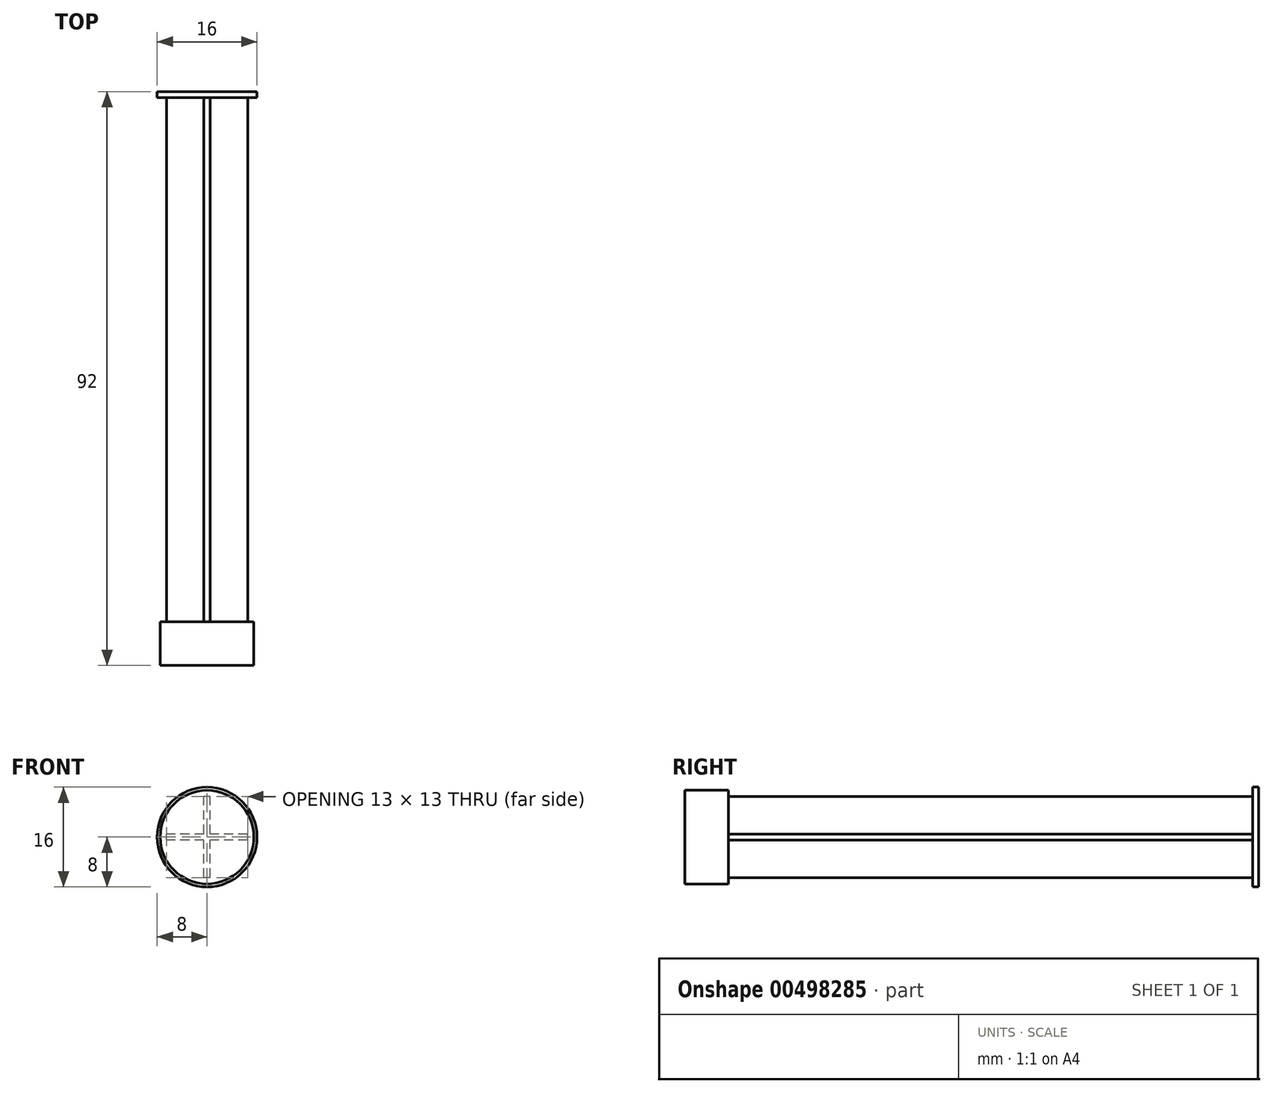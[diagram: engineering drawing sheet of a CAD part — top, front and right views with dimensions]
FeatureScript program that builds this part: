
annotation { "Feature Type Name" : "Feature", "Feature Type Description" : "" }
export const myFeature = defineFeature(function(context is Context, id is Id, definition is map)
    precondition{}
    {
        {
            var Q0;
            Q0=qCreatedBy(makeId("Front.planeOp"),FACE);
            var sketch = newSketch(context, id + "F0", { "sketchPlane" : qUnion([Q0])});
            skCircle(sketch, "E0", {"center": v(0, 0) * mm, "radius": 8 * mm});
            skSolve(sketch);
        }
        {
            var Q0;
            Q0 = qSketchRegion(id + "F0", true);
            var Q1;
            Q1=makeQuery(id+"F0.imprint","IMPRINT",FACE,{"disambiguationData":[TD([[makeQuery(id+"F0.imprint","IMPRINT",EDGE,{"derivedFrom":sQuery(id+"F0.wireOp",EDGE,"E0")}),1.0]])]});
            extrude(context, id + "F1", {"entities" : qUnion([Q0, Q1]), "depth" : 1 * mm});
        }
        {
            var Q0;
            Q0=makeQuery(id+"F1.opExtrude","CAP_FACE",FACE,{"disambiguationData":[OSD([sQuery(id+"F0.wireOp",EDGE,"E0")])],"isStart":false});
            var sketch = newSketch(context, id + "F2", { "sketchPlane" : qUnion([Q0])});
            skLineSegment(sketch, "E1", {"start": v(-6.5, 0) * mm, "end": v(6.5, 0) * mm});
            skLineSegment(sketch, "E2", {"start": v(0, 6.5) * mm, "end": v(0, -6.5) * mm});
            skLineSegment(sketch, "E3", {"start": v(-0.5, 0) * mm, "end": v(0.5, 0) * mm});
            skLineSegment(sketch, "E4", {"start": v(0, 0.5) * mm, "end": v(0, -0.5) * mm});
            skLineSegment(sketch, "E5.bottom", {"start": v(6.5, -0.5) * mm, "end": v(-6.5, -0.5) * mm});
            skLineSegment(sketch, "E5.top", {"start": v(6.5, 0.5) * mm, "end": v(-6.5, 0.5) * mm});
            skLineSegment(sketch, "E5.left", {"start": v(6.5, -0.5) * mm, "end": v(6.5, 0.5) * mm});
            skLineSegment(sketch, "E5.right", {"start": v(-6.5, -0.5) * mm, "end": v(-6.5, 0.5) * mm});
            skPoint(sketch, "E5.middle", {"position": v(0, 0) * mm});
            skLineSegment(sketch, "E6.bottom", {"start": v(0.5, -6.5) * mm, "end": v(-0.5, -6.5) * mm});
            skLineSegment(sketch, "E6.top", {"start": v(0.5, 6.5) * mm, "end": v(-0.5, 6.5) * mm});
            skLineSegment(sketch, "E6.left", {"start": v(0.5, -6.5) * mm, "end": v(0.5, 6.5) * mm});
            skLineSegment(sketch, "E6.right", {"start": v(-0.5, -6.5) * mm, "end": v(-0.5, 6.5) * mm});
            skSolve(sketch);
        }
        {
            var Q0;
            Q0 = qSketchRegion(id + "F2", true);
            extrude(context, id + "F3", {"entities" : qUnion([Q0]), "operationType" : NewBodyOperationType.ADD, "depth" : 84 * mm});
        }
        {
            var Q0;
            Q0=makeQuery(id+"F3.opExtrude","CAP_FACE",FACE,{"disambiguationData":[OSD([sQuery(id+"F2.wireOp",EDGE,"E5.bottom"),sQuery(id+"F2.wireOp",EDGE,"E5.top"),sQuery(id+"F2.wireOp",EDGE,"E5.left"),sQuery(id+"F2.wireOp",EDGE,"E5.right"),sQuery(id+"F2.wireOp",EDGE,"E6.bottom"),sQuery(id+"F2.wireOp",EDGE,"E6.top"),sQuery(id+"F2.wireOp",EDGE,"E6.left"),sQuery(id+"F2.wireOp",EDGE,"E6.right")])],"isStart":false});
            var sketch = newSketch(context, id + "F4", { "sketchPlane" : qUnion([Q0])});
            skCircle(sketch, "E7", {"center": v(0, 0) * mm, "radius": 7.5 * mm});
            skSolve(sketch);
        }
        {
            var Q0;
            Q0 = qSketchRegion(id + "F4", true);
            extrude(context, id + "F5", {"entities" : qUnion([Q0]), "operationType" : NewBodyOperationType.ADD, "depth" : 7 * mm});
        }
    });
